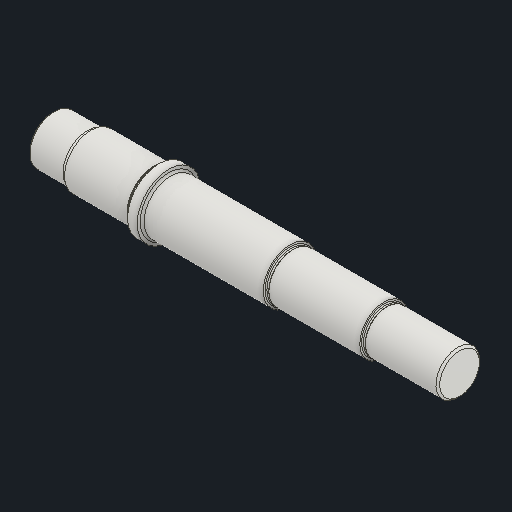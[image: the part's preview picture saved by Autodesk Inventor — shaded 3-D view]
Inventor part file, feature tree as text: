
AUTODESK INVENTOR PART (.ipt)
format: ipt  version: 2022 (Build 260153000, 153)  size: 245,248 bytes
history: native  units: mm
features: other x15, chamfer x2, fillet x2, revolve x1
ambient origin geometry x6: Origin, XZ Plane, XY Plane, X Axis, Y Axis, Z Axis
bodies: Body1 (feature_tree)
feature tree (20):
  other  "{BB8FE430-83BF-418D-8DF9-9B323D3DB9B9}"
  other  "Твердое тело1"
  revolve  "Вращение1"
  other  "Шпоночный паз1"
  other  "Шпоночный паз2"
  chamfer  "Фаска2"  [1 undecoded]
  fillet  "Сопряжение1"  Radius=50.0mm
  fillet  "Сопряжение2"  Radius=55.0mm
  other  "Просечка2"
  other  "Просечка3"
  chamfer  "Фаска3"  Distance=65.0mm
  other  "Просечка1"
  other  "Начальная плоскость"
  other  "Исходная точка"
  other  "Основной эскиз"
  other  "iFeature1:1"
  other  "iFeature1:2"
  other  "iFeature1:3"
  other  "iFeature11:1"
  other  "iFeature11:2"
note: 1 required parameter value undecoded (feature->parameter linkage not recoverable at this tier; creation-order binding heuristic only, values carry confidence <= 0.55)
